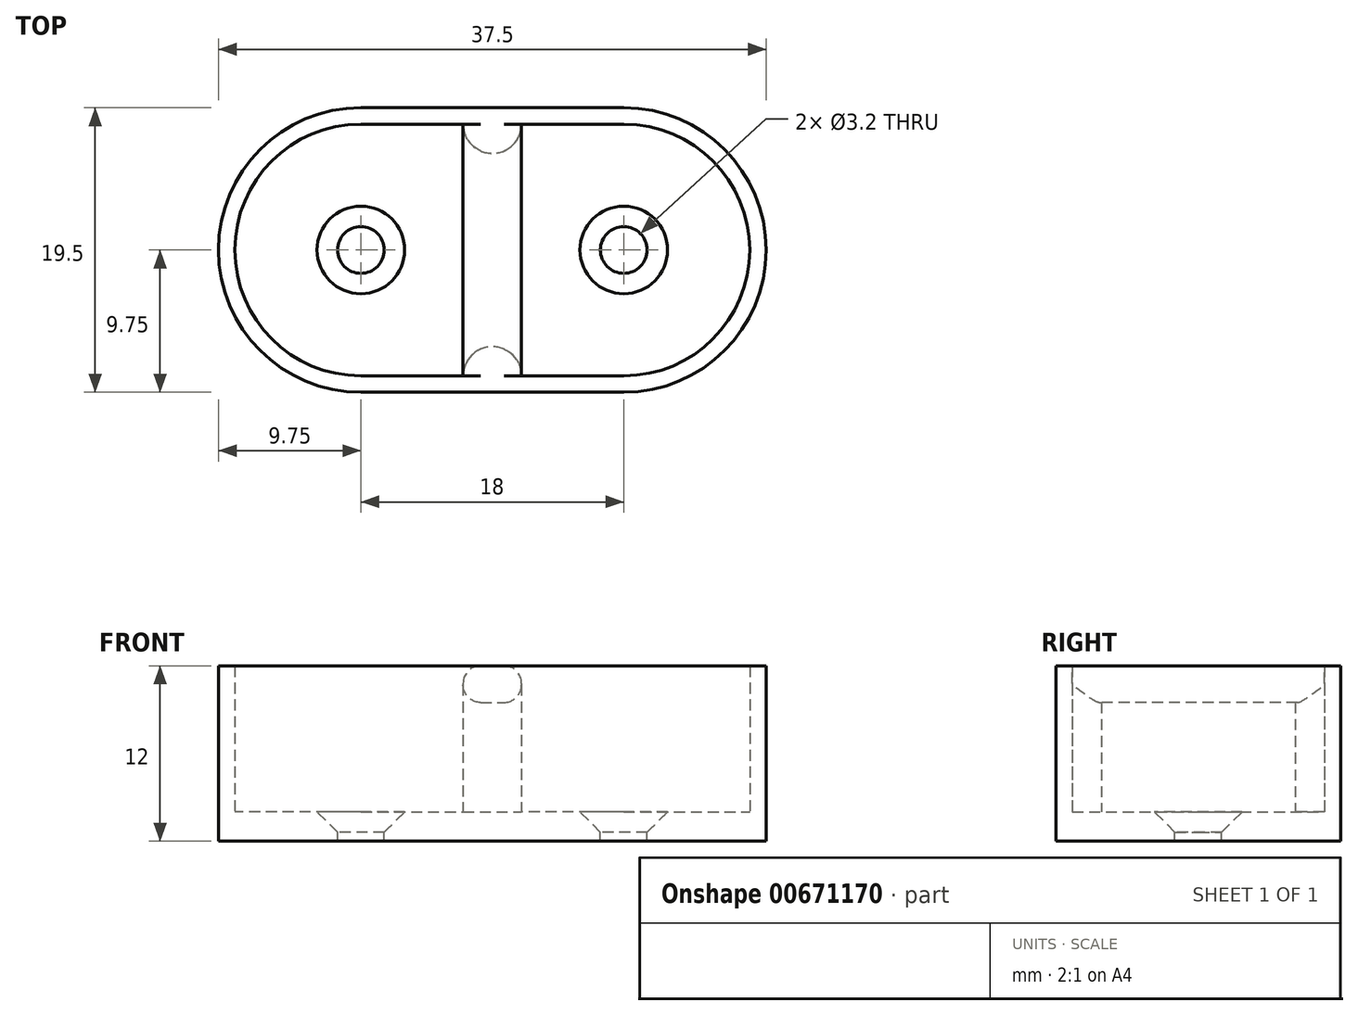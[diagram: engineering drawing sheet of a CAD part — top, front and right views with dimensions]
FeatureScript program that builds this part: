
annotation { "Feature Type Name" : "Feature", "Feature Type Description" : "" }
export const myFeature = defineFeature(function(context is Context, id is Id, definition is map)
    precondition{}
    {
        {
            var Q0;
            Q0=qCreatedBy(makeId("Top.planeOp"),FACE);
            var sketch = newSketch(context, id + "F0", { "sketchPlane" : qUnion([Q0])});
            skLineSegment(sketch, "E0", {"start": v(-9, 9.75) * mm, "end": v(9, 9.75) * mm});
            skLineSegment(sketch, "E1", {"start": v(9, -9.75) * mm, "end": v(-9, -9.75) * mm});
            skArc(sketch, "E2", {"start": v(9, -9.75) * mm, "mid": v(18.75, 0) * mm, "end": v(9, 9.75) * mm});
            skArc(sketch, "E3", {"start": v(-9, 9.75) * mm, "mid": v(-18.75, 0) * mm, "end": v(-9, -9.75) * mm});
            skSolve(sketch);
        }
        {
            var Q0;
            Q0 = qSketchRegion(id + "F0", true);
            extrude(context, id + "F1", {"entities" : qUnion([Q0]), "depth" : 2 * mm, "offsetDistance" : 25 * mm});
        }
        {
            var Q0;
            Q0=makeQuery(id+"F1.opExtrude","CAP_FACE",FACE,{"disambiguationData":[OSD([sQuery(id+"F0.wireOp",EDGE,"E0"),sQuery(id+"F0.wireOp",EDGE,"E1"),sQuery(id+"F0.wireOp",EDGE,"E2"),sQuery(id+"F0.wireOp",EDGE,"E3")])],"isStart":false});
            var sketch = newSketch(context, id + "F2", { "sketchPlane" : qUnion([Q0])});
            skLineSegment(sketch, "E4", {"start": v(-9, 9.75) * mm, "end": v(9, 9.75) * mm});
            skLineSegment(sketch, "E5", {"start": v(9, -9.75) * mm, "end": v(-9, -9.75) * mm});
            skArc(sketch, "E6", {"start": v(-9, 9.75) * mm, "mid": v(-18.75, 0) * mm, "end": v(-9, -9.75) * mm});
            skArc(sketch, "E7", {"start": v(9, -9.75) * mm, "mid": v(18.75, 0) * mm, "end": v(9, 9.75) * mm});
            skLineSegment(sketch, "E8", {"start": v(-9, 8.62) * mm, "end": v(-9, 8.62) * mm});
            skLineSegment(sketch, "E9", {"start": v(9, -8.62) * mm, "end": v(-9, -8.62) * mm});
            skLineSegment(sketch, "E10", {"start": v(-9, 8.62) * mm, "end": v(9, 8.62) * mm});
            skArc(sketch, "E11", {"start": v(-9, 8.62) * mm, "mid": v(-17.62, 0) * mm, "end": v(-9, -8.62) * mm});
            skArc(sketch, "E12", {"start": v(9, -8.62) * mm, "mid": v(17.62, 0) * mm, "end": v(9, 8.62) * mm});
            skSolve(sketch);
        }
        {
            var Q0;
            Q0 = qSketchRegion(id + "F2", true);
            extrude(context, id + "F3", {"entities" : qUnion([Q0]), "operationType" : NewBodyOperationType.ADD, "depth" : 10 * mm, "offsetDistance" : 25 * mm});
        }
        {
            var Q0;
            Q0=makeQuery(id+"F1.opExtrude","CAP_FACE",FACE,{"disambiguationData":[OSD([sQuery(id+"F0.wireOp",EDGE,"E0"),sQuery(id+"F0.wireOp",EDGE,"E1"),sQuery(id+"F0.wireOp",EDGE,"E2"),sQuery(id+"F0.wireOp",EDGE,"E3")])],"isStart":false});
            var sketch = newSketch(context, id + "F4", { "sketchPlane" : qUnion([Q0])});
            skArc(sketch, "E13", {"start": v(-2, 8.62) * mm, "mid": v(0, 6.63) * mm, "end": v(2, 8.62) * mm});
            skArc(sketch, "E14", {"start": v(2, -8.62) * mm, "mid": v(0, -6.63) * mm, "end": v(-2, -8.62) * mm});
            skLineSegment(sketch, "E15", {"start": v(-2, 8.62) * mm, "end": v(2, 8.62) * mm});
            skLineSegment(sketch, "E16", {"start": v(-2, -8.62) * mm, "end": v(2, -8.62) * mm});
            skSolve(sketch);
        }
        {
            var Q0;
            Q0 = qSketchRegion(id + "F4", true);
            extrude(context, id + "F5", {"entities" : qUnion([Q0]), "operationType" : NewBodyOperationType.ADD, "depth" : 10 * mm, "offsetDistance" : 25 * mm});
        }
        {
            var Q0;
            Q0=makeQuery(id+"F5.boolean.opBoolean","MERGE",FACE,{"derivedFrom":[makeQuery(id+"F3.opExtrude","CAP_FACE",FACE,{"disambiguationData":[OSD([sQuery(id+"F2.wireOp",EDGE,"E4"),sQuery(id+"F2.wireOp",EDGE,"E5"),sQuery(id+"F2.wireOp",EDGE,"E6"),sQuery(id+"F2.wireOp",EDGE,"E7"),sQuery(id+"F2.wireOp",EDGE,"E9"),sQuery(id+"F2.wireOp",EDGE,"E10"),sQuery(id+"F2.wireOp",EDGE,"E11"),sQuery(id+"F2.wireOp",EDGE,"E12")])],"isStart":false}),makeQuery(id+"F5.opExtrude","CAP_FACE",FACE,{"disambiguationData":[OSD([sQuery(id+"F4.wireOp",EDGE,"E13"),sQuery(id+"F4.wireOp",EDGE,"E15")])],"isStart":false}),makeQuery(id+"F5.opExtrude","CAP_FACE",FACE,{"disambiguationData":[OSD([sQuery(id+"F4.wireOp",EDGE,"E14"),sQuery(id+"F4.wireOp",EDGE,"E16")])],"isStart":false})]});
            cPlane(context, id + "F6", {"entities" : qUnion([Q0]), "cplaneType" : CPlaneType.OFFSET, "offset" : 2.5 * mm, "oppositeDirection" : true, "width" : 150 * mm, "height" : 150 * mm});
        }
        {
            var Q0;
            Q0=qCreatedBy(id+"F6.planeOp",FACE);
            var sketch = newSketch(context, id + "F7", { "sketchPlane" : qUnion([Q0])});
            skLineSegment(sketch, "E17", {"start": v(-2, 8.62) * mm, "end": v(-2, -8.62) * mm});
            skLineSegment(sketch, "E18", {"start": v(2, 8.62) * mm, "end": v(2, -8.62) * mm});
            skArc(sketch, "E19", {"start": v(-2, 8.62) * mm, "mid": v(0, 6.63) * mm, "end": v(2, 8.62) * mm});
            skArc(sketch, "E20", {"start": v(2, -8.62) * mm, "mid": v(0, -6.63) * mm, "end": v(-2, -8.62) * mm});
            skSolve(sketch);
        }
        {
            var Q0;
            Q0 = qSketchRegion(id + "F7", true);
            extrude(context, id + "F8", {"entities" : qUnion([Q0]), "operationType" : NewBodyOperationType.ADD, "depth" : 2.5 * mm, "offsetDistance" : 25 * mm});
        }
        {
            var Q0;
            Q0=makeQuery(id+"F8.opExtrude","CAP_EDGE",EDGE,{"disambiguationData":[OSD([sQuery(id+"F7.wireOp",EDGE,"E18")])],"isStart":false});
            var Q1;
            Q1=makeQuery(id+"F8.opExtrude","CAP_EDGE",EDGE,{"disambiguationData":[OSD([sQuery(id+"F7.wireOp",EDGE,"E17")])],"isStart":false});
            var Q2;
            Q2=makeQuery(id+"F8.opExtrude","CAP_EDGE",EDGE,{"disambiguationData":[OSD([sQuery(id+"F7.wireOp",EDGE,"E17")])],"isStart":true});
            var Q3;
            Q3=makeQuery(id+"F8.opExtrude","CAP_EDGE",EDGE,{"disambiguationData":[OSD([sQuery(id+"F7.wireOp",EDGE,"E18")])],"isStart":true});
            fillet(context, id + "F9", {"entities" : qUnion([Q0, Q1, Q2, Q3]), "radius" : 1.2 * mm, "tangentPropagation" : true, "allowEdgeOverflow" : false});
        }
        {
            var Q0;
            Q0=makeQuery(id+"F1.opExtrude","CAP_FACE",FACE,{"disambiguationData":[OSD([sQuery(id+"F0.wireOp",EDGE,"E0"),sQuery(id+"F0.wireOp",EDGE,"E1"),sQuery(id+"F0.wireOp",EDGE,"E2"),sQuery(id+"F0.wireOp",EDGE,"E3")])],"isStart":false});
            var sketch = newSketch(context, id + "F10", { "sketchPlane" : qUnion([Q0])});
            skPoint(sketch, "E21", {"position": v(-9, 0) * mm});
            skPoint(sketch, "E22", {"position": v(9, 0) * mm});
            skSolve(sketch);
        }
        {
            var Q0;
            Q0=sQuery(id+"F10.wireOp",VERTEX,"E21");
            var Q1;
            Q1=sQuery(id+"F10.wireOp",VERTEX,"E22");
            var Q2;
            Q2=makeQuery(id+"F1.opExtrude","SWEPT_BODY",BODY,{"disambiguationData":[OSD([sQuery(id+"F0.wireOp",EDGE,"E0"),sQuery(id+"F0.wireOp",EDGE,"E1"),sQuery(id+"F0.wireOp",EDGE,"E2"),sQuery(id+"F0.wireOp",EDGE,"E3")])]});
            hole(context, id + "F11", {"style" : HoleStyle.C_SINK, "endStyle" : HoleEndStyle.BLIND, "holeDiameter" : 3.2 * mm, "cSinkDiameter" : 6 * mm, "cSinkAngle" : 90 * degree, "majorDiameter" : 5 * mm, "holeDepth" : 4.5 * mm, "isTappedThrough" : true, "tappedDepth" : 12 * mm, "tapClearance" : 3, "startFromSketch" : true, "locations" : qUnion([Q0, Q1]), "scope" : qUnion([Q2])});
        }
    });
